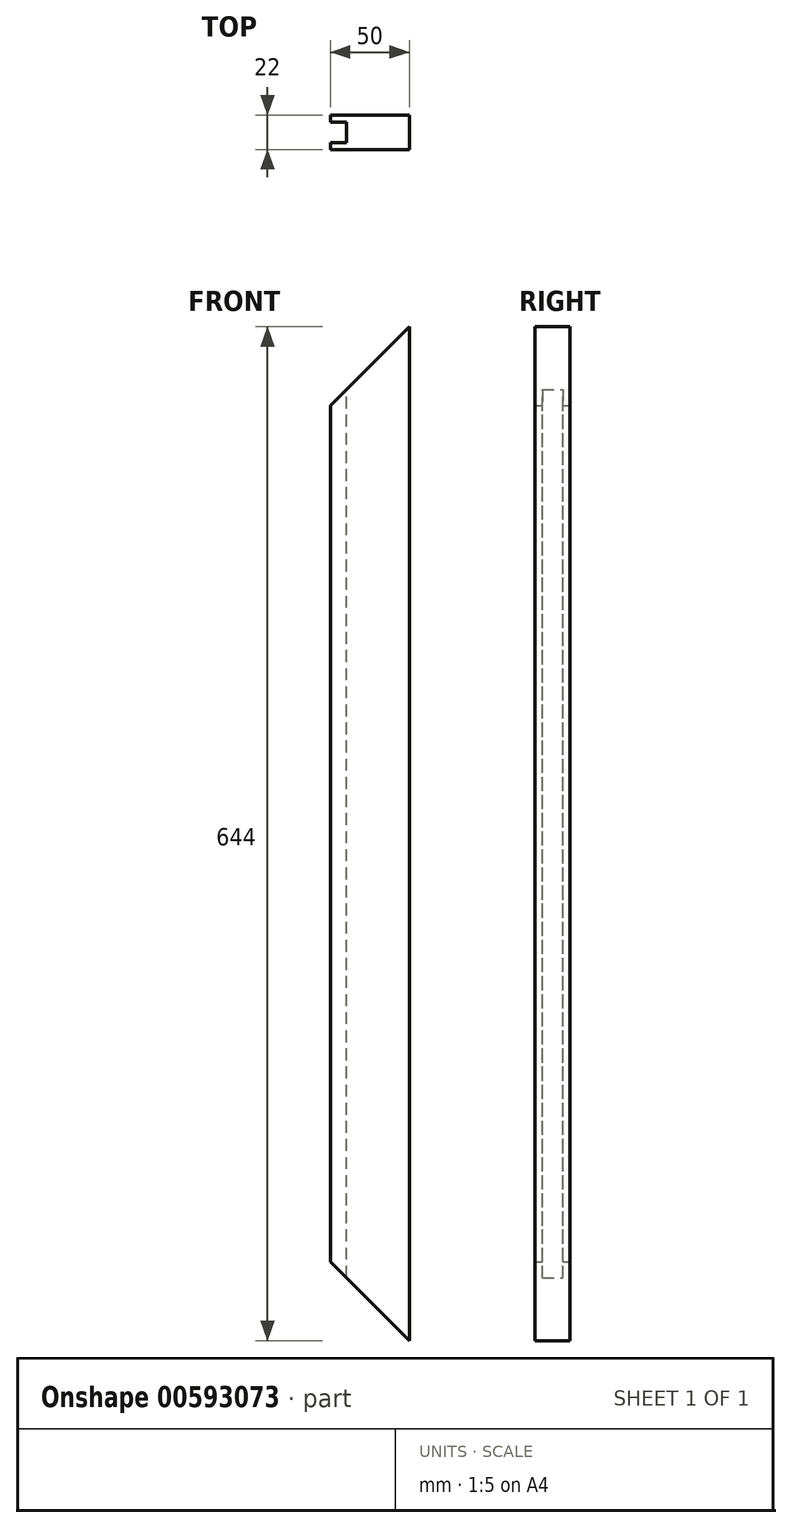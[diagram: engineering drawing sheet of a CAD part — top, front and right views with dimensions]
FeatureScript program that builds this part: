
annotation { "Feature Type Name" : "Feature", "Feature Type Description" : "" }
export const myFeature = defineFeature(function(context is Context, id is Id, definition is map)
    precondition{}
    {
        {
            var Q0;
            Q0=qCreatedBy(makeId("Front.planeOp"),FACE);
            var sketch = newSketch(context, id + "F0", { "sketchPlane" : qUnion([Q0])});
            skLineSegment(sketch, "E0.left", {"start": v(-50, 272) * mm, "end": v(-50, -272) * mm});
            skLineSegment(sketch, "E0.right", {"start": v(0, 322) * mm, "end": v(0, -322) * mm});
            skLineSegment(sketch, "E1", {"start": v(0, -322) * mm, "end": v(-50, -272) * mm});
            skLineSegment(sketch, "E2", {"start": v(0, 322) * mm, "end": v(-50, 272) * mm});
            skSolve(sketch);
        }
        {
            var Q0;
            Q0=makeQuery(id+"F0.imprint","IMPRINT",FACE,{"disambiguationData":[TD([[makeQuery(id+"F0.imprint","IMPRINT",EDGE,{"derivedFrom":sQuery(id+"F0.wireOp",EDGE,"E0.left")}),1.0]])]});
            extrude(context, id + "F1", {"entities" : qUnion([Q0]), "depth" : 22 * mm, "offsetDistance" : 25 * mm});
        }
        {
            var Q0;
            Q0=makeQuery(id+"F1.opExtrude","SWEPT_FACE",FACE,{"disambiguationData":[OSD([sQuery(id+"F0.wireOp",EDGE,"E0.left")])]});
            var sketch = newSketch(context, id + "F2", { "sketchPlane" : qUnion([Q0])});
            skLineSegment(sketch, "E3.bottom", {"start": v(4.5, -285.17) * mm, "end": v(17.5, -285.17) * mm});
            skLineSegment(sketch, "E3.top", {"start": v(4.5, 292.2) * mm, "end": v(17.5, 292.2) * mm});
            skLineSegment(sketch, "E3.left", {"start": v(4.5, -285.17) * mm, "end": v(4.5, 292.2) * mm});
            skLineSegment(sketch, "E3.right", {"start": v(17.5, -285.17) * mm, "end": v(17.5, 292.2) * mm});
            skSolve(sketch);
        }
        {
            var Q0;
            Q0 = qSketchRegion(id + "F2", true);
            extrude(context, id + "F3", {"entities" : qUnion([Q0]), "operationType" : NewBodyOperationType.REMOVE, "oppositeDirection" : true, "depth" : 10 * mm, "offsetDistance" : 25 * mm});
        }
    });
